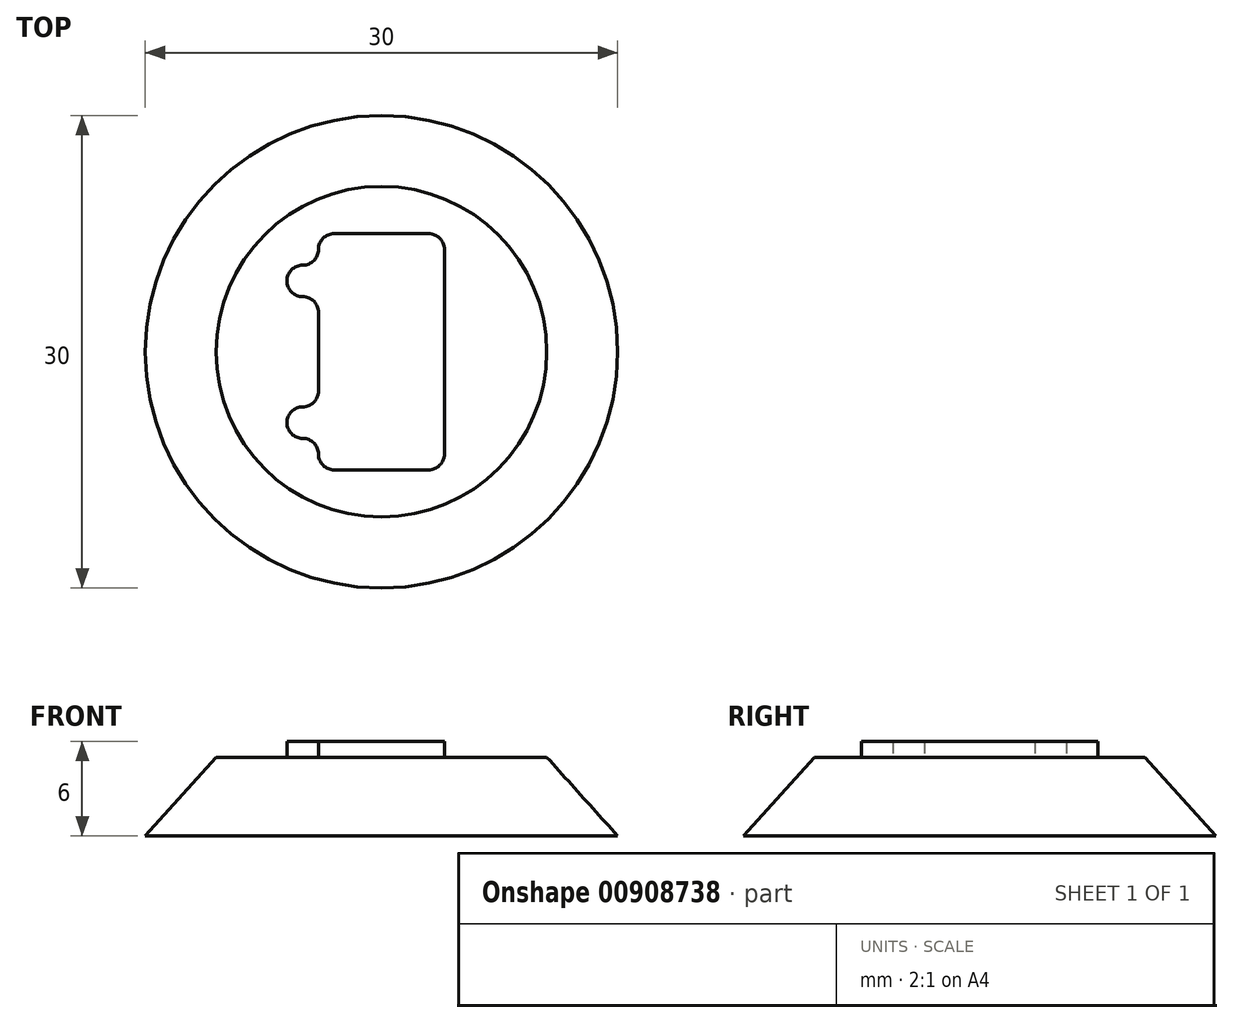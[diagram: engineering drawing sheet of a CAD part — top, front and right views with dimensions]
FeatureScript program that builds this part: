
annotation { "Feature Type Name" : "Feature", "Feature Type Description" : "" }
export const myFeature = defineFeature(function(context is Context, id is Id, definition is map)
    precondition{}
    {
        {
            var Q0;
            Q0=qCreatedBy(makeId("Top.planeOp"),FACE);
            var sketch = newSketch(context, id + "F0", { "sketchPlane" : qUnion([Q0])});
            skCircle(sketch, "E0", {"center": v(0, 0) * mm, "radius": 15 * mm});
            skSolve(sketch);
        }
        {
            var Q0;
            Q0=qCreatedBy(makeId("Top.planeOp"),FACE);
            cPlane(context, id + "F1", {"entities" : qUnion([Q0]), "cplaneType" : CPlaneType.OFFSET, "offset" : 5 * mm, "width" : 150 * mm, "height" : 150 * mm});
        }
        {
            var Q0;
            Q0=qCreatedBy(id+"F1.planeOp",FACE);
            var sketch = newSketch(context, id + "F2", { "sketchPlane" : qUnion([Q0])});
            skCircle(sketch, "E1", {"center": v(0, 0) * mm, "radius": 10.5 * mm});
            skSolve(sketch);
        }
        {
            var Q0;
            Q0=makeQuery(id+"F0.imprint","IMPRINT",FACE,{"disambiguationData":[TD([[makeQuery(id+"F0.imprint","IMPRINT",EDGE,{"derivedFrom":sQuery(id+"F0.wireOp",EDGE,"E0")}),1.0]])]});
            var Q1;
            Q1=makeQuery(id+"F2.imprint","IMPRINT",FACE,{"disambiguationData":[TD([[makeQuery(id+"F2.imprint","IMPRINT",EDGE,{"derivedFrom":sQuery(id+"F2.wireOp",EDGE,"E1")}),1.0]])]});
            loft(context, id + "F3", {"sheetProfilesArray" : [{ "sheetProfileEntities" : qUnion([Q0]) }, { "sheetProfileEntities" : qUnion([Q1]) }]});
        }
        {
            var Q0;
            Q0=makeQuery(id+"F3.opLoft","CAP_FACE",FACE,{"disambiguationData":[OSD([makeQuery(id+"F2.imprint","IMPRINT",FACE,{"disambiguationData":[TD([[makeQuery(id+"F2.imprint","IMPRINT",EDGE,{"derivedFrom":sQuery(id+"F2.wireOp",EDGE,"E1")}),1.0]])]})])],"isStart":true});
            var sketch = newSketch(context, id + "F4", { "sketchPlane" : qUnion([Q0])});
            skLineSegment(sketch, "E2.bottom", {"start": v(-4, -7.5) * mm, "end": v(4, -7.5) * mm});
            skLineSegment(sketch, "E2.top", {"start": v(-4, 7.5) * mm, "end": v(4, 7.5) * mm});
            skLineSegment(sketch, "E2.left", {"start": v(-4, -7.5) * mm, "end": v(-4, -5.5) * mm});
            skLineSegment(sketch, "E2.right", {"start": v(4, -7.5) * mm, "end": v(4, 7.5) * mm});
            skLineSegment(sketch, "E3", {"start": v(-4, -7.5) * mm, "end": v(4, 7.5) * mm, "construction": true});
            skLineSegment(sketch, "E4", {"start": v(-4, 5.5) * mm, "end": v(-6, 5.5) * mm});
            skLineSegment(sketch, "E5", {"start": v(-6, 5.5) * mm, "end": v(-6, 3.5) * mm});
            skLineSegment(sketch, "E6", {"start": v(-6, 3.5) * mm, "end": v(-4, 3.5) * mm});
            skLineSegment(sketch, "E7.MirrorCS", {"start": v(-6, -3.5) * mm, "end": v(-4, -3.5) * mm});
            skLineSegment(sketch, "E8.MirrorCS", {"start": v(-6, -5.5) * mm, "end": v(-6, -3.5) * mm});
            skLineSegment(sketch, "E9.MirrorCS", {"start": v(-4, -5.5) * mm, "end": v(-6, -5.5) * mm});
            skLineSegment(sketch, "E10.MirrorCS", {"start": v(-4, 7.5) * mm, "end": v(-4, 5.5) * mm});
            skLineSegment(sketch, "E11.trimOffspring", {"start": v(-4, 3.5) * mm, "end": v(-4, -3.5) * mm});
            skLineSegment(sketch, "E12.trimOffspring", {"start": v(-4, -5.5) * mm, "end": v(-4, -7.5) * mm});
            skLineSegment(sketch, "E13.trimOffspring", {"start": v(-4, 5.5) * mm, "end": v(-4, 7.5) * mm});
            skLineSegment(sketch, "E14.trimOffspring", {"start": v(-4, -3.5) * mm, "end": v(-4, 3.5) * mm});
            skSolve(sketch);
        }
        {
            var Q0;
            Q0 = qSketchRegion(id + "F4", true);
            extrude(context, id + "F5", {"entities" : qUnion([Q0]), "operationType" : NewBodyOperationType.ADD, "depth" : 1 * mm, "offsetDistance" : 25 * mm});
        }
        {
            var Q0;
            Q0=makeQuery(id+"F5.opExtrude","SWEPT_EDGE",EDGE,{"disambiguationData":[OSD([sQuery(id+"F4.wireOp",EDGE,"E2.bottom"),sQuery(id+"F4.wireOp",EDGE,"E12.trimOffspring")])]});
            var Q1;
            Q1=makeQuery(id+"F5.opExtrude","SWEPT_EDGE",EDGE,{"disambiguationData":[OSD([sQuery(id+"F4.wireOp",EDGE,"E2.bottom"),sQuery(id+"F4.wireOp",EDGE,"E2.right")])]});
            var Q2;
            Q2=makeQuery(id+"F5.opExtrude","SWEPT_EDGE",EDGE,{"disambiguationData":[OSD([sQuery(id+"F4.wireOp",EDGE,"E2.top"),sQuery(id+"F4.wireOp",EDGE,"E2.right")])]});
            var Q3;
            Q3=makeQuery(id+"F5.opExtrude","SWEPT_EDGE",EDGE,{"disambiguationData":[OSD([sQuery(id+"F4.wireOp",EDGE,"E2.top"),sQuery(id+"F4.wireOp",EDGE,"E13.trimOffspring")])]});
            var Q4;
            Q4=makeQuery(id+"F5.opExtrude","SWEPT_EDGE",EDGE,{"disambiguationData":[OSD([sQuery(id+"F4.wireOp",EDGE,"E9.MirrorCS"),sQuery(id+"F4.wireOp",EDGE,"E12.trimOffspring")])]});
            var Q5;
            Q5=makeQuery(id+"F5.opExtrude","SWEPT_EDGE",EDGE,{"disambiguationData":[OSD([sQuery(id+"F4.wireOp",EDGE,"E6"),sQuery(id+"F4.wireOp",EDGE,"E14.trimOffspring")])]});
            var Q6;
            Q6=makeQuery(id+"F5.opExtrude","SWEPT_EDGE",EDGE,{"disambiguationData":[OSD([sQuery(id+"F4.wireOp",EDGE,"E7.MirrorCS"),sQuery(id+"F4.wireOp",EDGE,"E14.trimOffspring")])]});
            var Q7;
            Q7=makeQuery(id+"F5.opExtrude","SWEPT_EDGE",EDGE,{"disambiguationData":[OSD([sQuery(id+"F4.wireOp",EDGE,"E4"),sQuery(id+"F4.wireOp",EDGE,"E13.trimOffspring")])]});
            fillet(context, id + "F6", {"entities" : qUnion([Q0, Q1, Q2, Q3, Q4, Q5, Q6, Q7]), "radius" : 1 * mm, "tangentPropagation" : true, "allowEdgeOverflow" : false});
        }
    });
